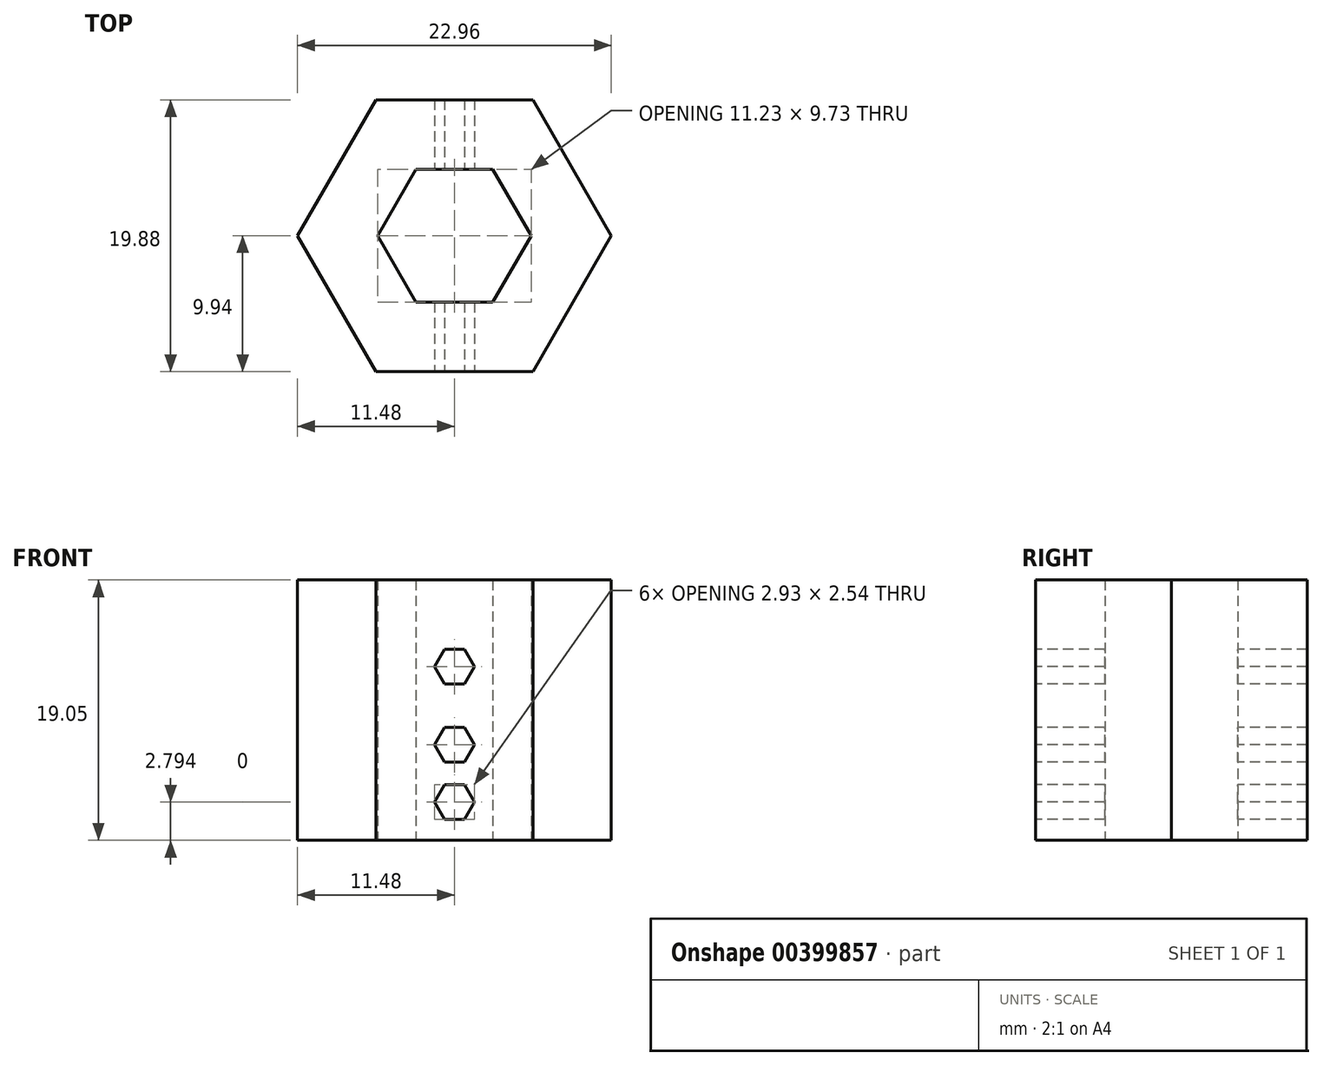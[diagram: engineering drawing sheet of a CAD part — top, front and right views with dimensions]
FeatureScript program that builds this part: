
annotation { "Feature Type Name" : "Feature", "Feature Type Description" : "" }
export const myFeature = defineFeature(function(context is Context, id is Id, definition is map)
    precondition{}
    {
        {
            var Q0;
            Q0=qCreatedBy(makeId("Top.planeOp"),FACE);
            var sketch = newSketch(context, id + "F0", { "sketchPlane" : qUnion([Q0])});
            skCircle(sketch, "E0.cCircle", {"center": v(0, 0) * mm, "radius": 4.86 * mm, "construction": true});
            skLineSegment(sketch, "E0.0", {"start": v(-2.8, 4.86) * mm, "end": v(2.8, 4.86) * mm});
            skLineSegment(sketch, "E0.1", {"start": v(2.8, 4.86) * mm, "end": v(5.62, 0) * mm});
            skLineSegment(sketch, "E0.2", {"start": v(5.62, 0) * mm, "end": v(2.8, -4.86) * mm});
            skLineSegment(sketch, "E0.3", {"start": v(2.8, -4.86) * mm, "end": v(-2.8, -4.86) * mm});
            skLineSegment(sketch, "E0.4", {"start": v(-2.8, -4.86) * mm, "end": v(-5.62, 0) * mm});
            skLineSegment(sketch, "E0.5", {"start": v(-5.62, 0) * mm, "end": v(-2.8, 4.86) * mm});
            skPoint(sketch, "E0.0.midPoint", {"position": v(0, 4.86) * mm});
            skLineSegment(sketch, "E1.0", {"start": v(-5.74, 9.94) * mm, "end": v(5.74, 9.94) * mm});
            skLineSegment(sketch, "E1.1", {"start": v(11.48, 0) * mm, "end": v(5.74, -9.94) * mm});
            skLineSegment(sketch, "E1.2", {"start": v(5.74, -9.94) * mm, "end": v(-5.74, -9.94) * mm});
            skLineSegment(sketch, "E1.3", {"start": v(5.74, 9.94) * mm, "end": v(11.48, 0) * mm});
            skLineSegment(sketch, "E1.4", {"start": v(-5.74, -9.94) * mm, "end": v(-11.48, 0) * mm});
            skLineSegment(sketch, "E1.5", {"start": v(-11.48, 0) * mm, "end": v(-5.74, 9.94) * mm});
            skSolve(sketch);
        }
        {
            var Q0;
            Q0=makeQuery(id+"F0.imprint","IMPRINT",FACE,{"disambiguationData":[TD([[makeQuery(id+"F0.imprint","IMPRINT",EDGE,{"derivedFrom":sQuery(id+"F0.wireOp",EDGE,"E0.0")}),1.0]])]});
            extrude(context, id + "F1", {"entities" : qUnion([Q0]), "depth" : 19.05 * mm});
        }
        {
            var Q0;
            Q0=makeQuery(id+"F1.opExtrude","SWEPT_FACE",FACE,{"disambiguationData":[OSD([sQuery(id+"F0.wireOp",EDGE,"E1.2")])]});
            var sketch = newSketch(context, id + "F2", { "sketchPlane" : qUnion([Q0])});
            skLineSegment(sketch, "E2.0", {"start": v(5.74, 19.05) * mm, "end": v(-5.74, 19.05) * mm, "construction": true});
            skLineSegment(sketch, "E2.1", {"start": v(5.74, 0) * mm, "end": v(-5.74, 0) * mm, "construction": true});
            skCircle(sketch, "E3.cCircle", {"center": v(0, 12.7) * mm, "radius": 1.27 * mm, "construction": true});
            skPoint(sketch, "E3.cCircle.centerSnap0", {"position": v(0, 19.05) * mm});
            skLineSegment(sketch, "E3.0", {"start": v(-0.73, 13.97) * mm, "end": v(0.73, 13.97) * mm});
            skLineSegment(sketch, "E3.1", {"start": v(0.73, 13.97) * mm, "end": v(1.47, 12.7) * mm});
            skLineSegment(sketch, "E3.2", {"start": v(1.47, 12.7) * mm, "end": v(0.73, 11.43) * mm});
            skLineSegment(sketch, "E3.3", {"start": v(0.73, 11.43) * mm, "end": v(-0.73, 11.43) * mm});
            skLineSegment(sketch, "E3.4", {"start": v(-0.73, 11.43) * mm, "end": v(-1.47, 12.7) * mm});
            skLineSegment(sketch, "E3.5", {"start": v(-1.47, 12.7) * mm, "end": v(-0.73, 13.97) * mm});
            skPoint(sketch, "E3.0.midPoint", {"position": v(0, 13.97) * mm});
            skCircle(sketch, "E4.cCircle", {"center": v(0, 2.8) * mm, "radius": 1.27 * mm, "construction": true});
            skLineSegment(sketch, "E4.0", {"start": v(-0.73, 4.06) * mm, "end": v(0.73, 4.06) * mm});
            skLineSegment(sketch, "E4.1", {"start": v(0.73, 4.06) * mm, "end": v(1.47, 2.8) * mm});
            skLineSegment(sketch, "E4.2", {"start": v(1.47, 2.8) * mm, "end": v(0.73, 1.52) * mm});
            skLineSegment(sketch, "E4.3", {"start": v(0.73, 1.52) * mm, "end": v(-0.73, 1.52) * mm});
            skLineSegment(sketch, "E4.4", {"start": v(-0.73, 1.52) * mm, "end": v(-1.47, 2.8) * mm});
            skLineSegment(sketch, "E4.5", {"start": v(-1.47, 2.8) * mm, "end": v(-0.73, 4.06) * mm});
            skPoint(sketch, "E4.0.midPoint", {"position": v(0, 4.06) * mm});
            skCircle(sketch, "E5.cCircle", {"center": v(0, 6.99) * mm, "radius": 1.27 * mm, "construction": true});
            skLineSegment(sketch, "E5.0", {"start": v(-0.73, 8.26) * mm, "end": v(0.73, 8.26) * mm});
            skLineSegment(sketch, "E5.1", {"start": v(0.73, 8.26) * mm, "end": v(1.47, 6.99) * mm});
            skLineSegment(sketch, "E5.2", {"start": v(1.47, 6.99) * mm, "end": v(0.73, 5.71) * mm});
            skLineSegment(sketch, "E5.3", {"start": v(0.73, 5.72) * mm, "end": v(-0.73, 5.72) * mm});
            skLineSegment(sketch, "E5.4", {"start": v(-0.73, 5.71) * mm, "end": v(-1.47, 6.99) * mm});
            skLineSegment(sketch, "E5.5", {"start": v(-1.47, 6.99) * mm, "end": v(-0.73, 8.26) * mm});
            skPoint(sketch, "E5.0.midPoint", {"position": v(0, 8.26) * mm});
            skSolve(sketch);
        }
        {
            var Q0;
            Q0=makeQuery(id+"F2.imprint","IMPRINT",FACE,{"disambiguationData":[TD([[makeQuery(id+"F2.imprint","IMPRINT",EDGE,{"derivedFrom":sQuery(id+"F2.wireOp",EDGE,"E3.0")}),-1.0]])]});
            var Q1;
            Q1=makeQuery(id+"F2.imprint","IMPRINT",FACE,{"disambiguationData":[TD([[makeQuery(id+"F2.imprint","IMPRINT",EDGE,{"derivedFrom":sQuery(id+"F2.wireOp",EDGE,"E5.0")}),-1.0]])]});
            var Q2;
            Q2=makeQuery(id+"F2.imprint","IMPRINT",FACE,{"disambiguationData":[TD([[makeQuery(id+"F2.imprint","IMPRINT",EDGE,{"derivedFrom":sQuery(id+"F2.wireOp",EDGE,"E4.0")}),-1.0]])]});
            extrude(context, id + "F3", {"entities" : qUnion([Q0, Q1, Q2]), "operationType" : NewBodyOperationType.REMOVE, "endBound" : BoundingType.THROUGH_ALL, "oppositeDirection" : true, "depth" : 25.4 * mm});
        }
    });
